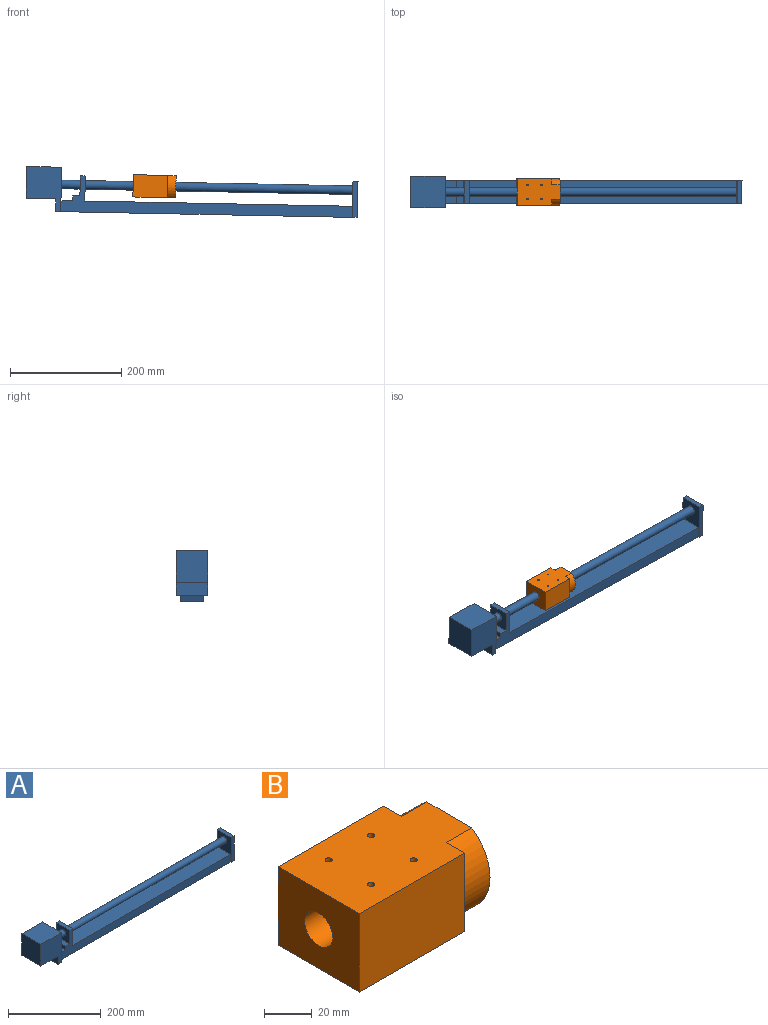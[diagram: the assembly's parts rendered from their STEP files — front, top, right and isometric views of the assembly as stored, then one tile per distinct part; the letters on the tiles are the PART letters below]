
ASSEMBLY  parts=2 mates=1
PART A: 24 faces, bbox 597x57x80 mm
  f0: plane 482x40mm, normal (0,0,1), area 19280mm2, adj f8,f9,f10,f20
  f1: cylinder r=7.75mm len=482mm, axis (-1,0,0), area 23470.8mm2, adj f8,f20
  f2: cylinder r=7.75mm len=34mm, axis (-1,0,0), area 1655.6mm2, adj f12,f22
  f3: plane 65x9mm, normal (0,1,0), area 585mm2, adj f4,f6,f7,f8
  f4: plane 42x9mm, normal (0,0,1), area 378mm2, adj f3,f5,f7,f8
  f5: plane 65x9mm, normal (0,-1,0), area 585mm2, adj f4,f6,f7,f8
  f6: plane 543x57mm, normal (0,0,-1), area 21891mm2, adj f3,f5,f7,f8,f9,f10,f12,f13
  f7: plane 65x42mm, normal (1,0,0), area 2730mm2, adj f3,f4,f5,f6
  f8: plane 65x42mm, normal (-1,0,0), area 1741.3mm2, adj f0,f1,f3,f4,f5,f6,f9,f10
  f9: plane 525x65mm, normal (0,1,0), area 11022mm2, adj f0,f6,f8,f11,f12,f19,f20,f21
  f10: plane 525x65mm, normal (0,-1,0), area 11022mm2, adj f0,f6,f8,f11,f12,f19,f20,f21
  f11: plane 40x21mm, normal (0,0,1), area 840mm2, adj f9,f10,f12,f19
  f12: plane 80x57mm, normal (1,0,0), area 3571.3mm2, adj f2,f6,f9,f10,f11,f13,f14,f15
  f13: plane 80x63mm, normal (0,-1,0), area 3798mm2, adj f6,f12,f14,f16,f17,f18
  f14: plane 63x57mm, normal (0,0,1), area 3591mm2, adj f12,f13,f15,f18
  f15: plane 80x63mm, normal (0,1,0), area 3798mm2, adj f6,f12,f14,f16,f17,f18
  f16: plane 57x23mm, normal (-1,0,0), area 1311mm2, adj f6,f13,f15,f17
  f17: plane 57x54mm, normal (0,0,-1), area 3078mm2, adj f13,f15,f16,f18
  f18: plane 57x57mm, normal (-1,0,0), area 3249mm2, adj f13,f14,f15,f17
  f19: plane 40x9mm, normal (-1,0,0), area 360mm2, adj f9,f10,f11,f23
  f20: plane 45x40mm, normal (1,0,0), area 1611.3mm2, adj f0,f1,f9,f10,f21
  f21: plane 40x9mm, normal (0,0,1), area 360mm2, adj f9,f10,f20,f22
  f22: plane 40x36mm, normal (-1,0,0), area 1251.3mm2, adj f2,f9,f10,f21,f23
  f23: plane 40x13mm, normal (0,0,1), area 520mm2, adj f9,f10,f19,f22
PART B: 21 faces, bbox 77x48x40 mm
  f0: plane 20x10.73mm, normal (1,0,0), area 63.6mm2, adj f6,f8,f9
  f1: plane 20x10.73mm, normal (1,0,0), area 63.6mm2, adj f6,f7,f9
  f2: plane 20x10.73mm, normal (1,0,0), area 63.6mm2, adj f4,f7,f10
  f3: plane 20x10.73mm, normal (1,0,0), area 63.6mm2, adj f4,f8,f10
  f4: plane 62x40mm, normal (0,1,0), area 2480mm2, adj f2,f3,f5,f7,f8
  f5: plane 48x40mm, normal (-1,0,0), area 1706.2mm2, adj f4,f6,f7,f8,f12
  f6: plane 62x40mm, normal (0,-1,0), area 2480mm2, adj f0,f1,f5,f7,f8
  f7: plane 77x48mm, normal (0,0,-1), area 3374mm2, adj f1,f2,f4,f5,f6,f9,f10,f11
  f8: plane 77x48mm, normal (0,0,1), area 3345.7mm2, adj f0,f3,f4,f5,f6,f9,f10,f11
  f9: cylinder r=24mm len=40mm, axis (-1,0,0), area 709.3mm2, adj f0,f1,f7,f8,f11
  f10: cylinder r=24mm len=40mm, axis (-1,0,0), area 709.3mm2, adj f2,f3,f7,f8,f11
  f11: plane 48x40mm, normal (1,0,0), area 1451.7mm2, adj f7,f8,f9,f10,f12
  f12: cylinder r=8.25mm len=77mm, axis (1,0,0), area 3991.4mm2, adj f5,f11
  f13: cone r=0mm half-angle=59deg, axis (0,0,1), area 8.2mm2, adj f14
  f14: cylinder r=1.5mm len=12mm, axis (0,0,1), area 113.1mm2, adj f8,f13
  f15: cone r=0mm half-angle=59deg, axis (0,0,1), area 8.2mm2, adj f16
  f16: cylinder r=1.5mm len=12mm, axis (0,0,1), area 113.1mm2, adj f8,f15
  f17: cone r=0mm half-angle=59deg, axis (0,0,1), area 8.2mm2, adj f18
  f18: cylinder r=1.5mm len=12mm, axis (0,0,1), area 113.1mm2, adj f8,f17
  f19: cone r=0mm half-angle=59deg, axis (0,0,1), area 8.2mm2, adj f20
  f20: cylinder r=1.5mm len=12mm, axis (0,0,1), area 113.1mm2, adj f8,f19
PLACE A rot(axis=(0,1,0),1.1deg) t=(204.05,88.87,-18.9)mm
PLACE B rot(axis=(0,1,0),1.1deg) t=(364.4,88.87,-22.05)mm
MATE slider B.f9 <-> A.f1  axis (1,0,-0.02) through (410,88.87,-42.95)mm
